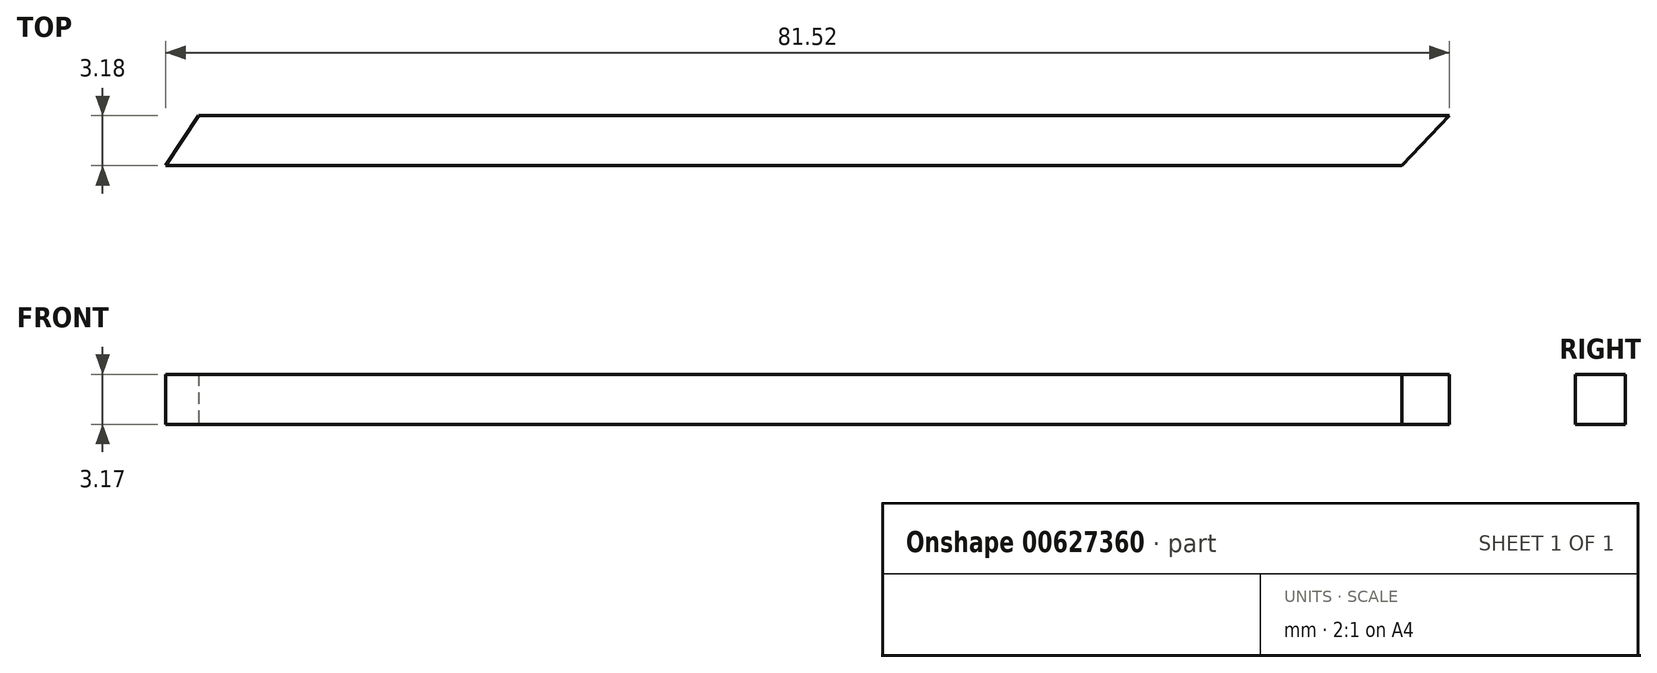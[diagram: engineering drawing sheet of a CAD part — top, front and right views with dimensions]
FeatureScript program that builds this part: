
annotation { "Feature Type Name" : "Feature", "Feature Type Description" : "" }
export const myFeature = defineFeature(function(context is Context, id is Id, definition is map)
    precondition{}
    {
        {
            var Q0;
            Q0=qCreatedBy(makeId("Top.planeOp"),FACE);
            var sketch = newSketch(context, id + "F0", { "sketchPlane" : qUnion([Q0])});
            skLineSegment(sketch, "E0", {"start": v(-79.44, 3.18) * mm, "end": v(0, 3.18) * mm});
            skLineSegment(sketch, "E1", {"start": v(0, 3.18) * mm, "end": v(-3.01, 0) * mm});
            skLineSegment(sketch, "E2", {"start": v(-3.01, 0) * mm, "end": v(-81.52, 0) * mm});
            skLineSegment(sketch, "E3", {"start": v(-81.52, 0) * mm, "end": v(-79.44, 3.18) * mm});
            skSolve(sketch);
        }
        {
            var Q0;
            Q0=makeQuery(id+"F0.imprint","IMPRINT",FACE,{"disambiguationData":[TD([[makeQuery(id+"F0.imprint","IMPRINT",EDGE,{"derivedFrom":sQuery(id+"F0.wireOp",EDGE,"E0")}),-1.0]])]});
            extrude(context, id + "F1", {"entities" : qUnion([Q0]), "depth" : 3.17 * mm, "offsetDistance" : 25.4 * mm});
        }
    });
